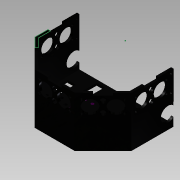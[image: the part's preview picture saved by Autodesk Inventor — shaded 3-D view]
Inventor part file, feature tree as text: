
AUTODESK INVENTOR PART (.ipt)
format: ipt  version: 2015 SP1 (Build 190203100, 203)  size: 460,288 bytes
history: native  units: mm
features: reference x56, sketch x20, extrude x20, projected_geometry x3
ambient origin geometry x8: Origin, YZ Plane, XZ Plane, XY Plane, X Axis, Y Axis, Z Axis, Center Point
bodies: Body1 (feature_tree)
feature tree (99):
  sketch  "Sketch1"  dims[d64=3.0mm d65=0.0mm d68=60.0mm d69=0.0mm]
  extrude  "Extrusion8"  Depth=60.0mm TaperAngle=0.0deg
  extrude  "Extrusion9"  Depth=3.5mm
  extrude  "Extrusion10"  Depth=3.5mm
  extrude  "Extrusion11"  Depth=3.5mm
  extrude  "Extrusion12"  Depth=10.0mm
  extrude  "Extrusion19"  Depth=17.5mm
  extrude  "Extrusion22"  Depth=17.5mm
  extrude  "Extrusion23"  Depth=10.0mm
  sketch  "Sketch22"  dims[d141=10.0mm d144=1.65mm]
  extrude  "Extrusion27"  Depth=10.0mm TaperAngle=0.0deg
  extrude  "Extrusion30"  Depth=3.5mm
  extrude  "Extrusion31"  Depth=7.0mm
  extrude  "Extrusion32"  Depth=7.0mm
  extrude  "Extrusion33"  Depth=10.0mm TaperAngle=0.0deg
  extrude  "Extrusion36"  Depth=17.5mm
  extrude  "Extrusion40"  Depth=3.0mm TaperAngle=0.0deg
  extrude  "Extrusion41"  Depth=120.811657mm
  extrude  "Extrusion42"  Depth=50.041827mm
  extrude  "Extrusion43"  Depth=52.663858mm
  extrude  "Extrusion44"  Depth=3.0mm
  extrude  "Extrusion45"  Depth=10.0mm
  sketch  "Sketch41"  dims[d206=47.556546mm d207=47.556546mm d208=47.556546mm d209=51.421217mm d210=135.0deg d211=135.0deg d212=135.0deg d213=135.0deg d214=135.0deg d215=135.0deg d216=135.0deg d217=135.0deg d218=3.0mm d219=3.0mm d220=3.0mm d221=3.0mm d222=0.0mm d223=17.500137mm d225=3.0mm d231=0.0mm d232=3.0mm d233=0.0mm d234=3.0mm d235=0.0mm d236=3.0mm d237=0.0mm d242=3.5mm d243=3.5mm d244=10.0mm d245=0.0mm d252=10.0mm d253=0.0mm d254=10.0mm d255=0.0mm d256=180.0mm d257=0.0mm d258=180.0mm d259=0.0mm d260=180.0mm d261=0.0mm d262=3.5mm d263=3.5mm d264=3.5mm d265=3.5mm d266=10.0mm d267=0.0mm]
  sketch  "Sketch10"  dims[d115=3.5mm d116=3.5mm]
  sketch  "Sketch11"  dims[d117=3.5mm d118=3.5mm]
  reference  "Reference28"
  reference  "Reference29"
  reference  "Reference30"
  reference  "Reference31"
  reference  "Reference32"
  reference  "Reference33"
  reference  "Reference34"
  sketch  "Sketch12"  dims[d119=3.5mm d120=3.5mm]
  reference  "Reference35"
  reference  "Reference36"
  sketch  "Sketch18"  dims[d127=10.0mm d128=0.0mm d129=10.0mm]
  sketch  "Sketch20"  dims[d130=17.5mm d132=17.5mm]
  reference  "Reference75"
  reference  "Reference76"
  sketch  "Sketch21"  dims[d133=15.0mm d136=17.5mm d137=10.0mm]
  sketch  "Sketch23"  dims[d145=10.0mm d146=0.0mm d147=10.0mm d148=0.0mm]
  reference  "Reference79"
  reference  "Reference80"
  reference  "Reference81"
  reference  "Reference82"
  sketch  "Sketch26"  dims[d161=3.5mm d162=3.5mm]
  reference  "Reference83"
  reference  "Reference84"
  reference  "Reference85"
  reference  "Reference86"
  reference  "Reference87"
  reference  "Reference88"
  reference  "Reference89"
  reference  "Reference90"
  projected_geometry  "Projected Loop2"
  sketch  "Sketch27"  dims[d163=7.0mm d164=7.0mm]
  sketch  "Sketch28"  dims[d165=7.0mm d166=7.0mm]
  projected_geometry  "Projected Loop3"
  sketch  "Sketch31"  dims[d167=10.0mm d168=0.0mm d173=10.0mm d174=0.0mm]
  sketch  "Sketch34"  dims[d175=10.0mm d176=0.0mm d181=17.5mm]
  reference  "Reference97"
  reference  "Reference98"
  reference  "Reference99"
  reference  "Reference100"
  reference  "Reference101"
  reference  "Reference102"
  reference  "Reference103"
  reference  "Reference104"
  sketch  "Sketch35"  dims[d186=10.0mm d187=0.0mm d193=3.0mm d194=0.0mm]
  reference  "Reference105"
  reference  "Reference106"
  reference  "Reference107"
  reference  "Reference108"
  reference  "Reference109"
  reference  "Reference110"
  reference  "Reference111"
  reference  "Reference112"
  sketch  "Sketch36"  dims[d195=120.811657mm d198=50.041827mm]
  reference  "Reference113"
  reference  "Reference114"
  reference  "Reference115"
  reference  "Reference116"
  reference  "Reference117"
  reference  "Reference118"
  reference  "Reference119"
  reference  "Reference120"
  sketch  "Sketch37"  dims[d199=50.041827mm d200=50.041827mm]
  reference  "Reference121"
  reference  "Reference122"
  reference  "Reference123"
  reference  "Reference124"
  reference  "Reference125"
  reference  "Reference126"
  reference  "Reference127"
  reference  "Reference128"
  sketch  "Sketch38"  dims[d201=52.663858mm d202=52.663858mm]
  reference  "Reference129"
  sketch  "Sketch40"  dims[d204=3.0mm d205=51.421217mm]
  projected_geometry  "Projected Loop5"
